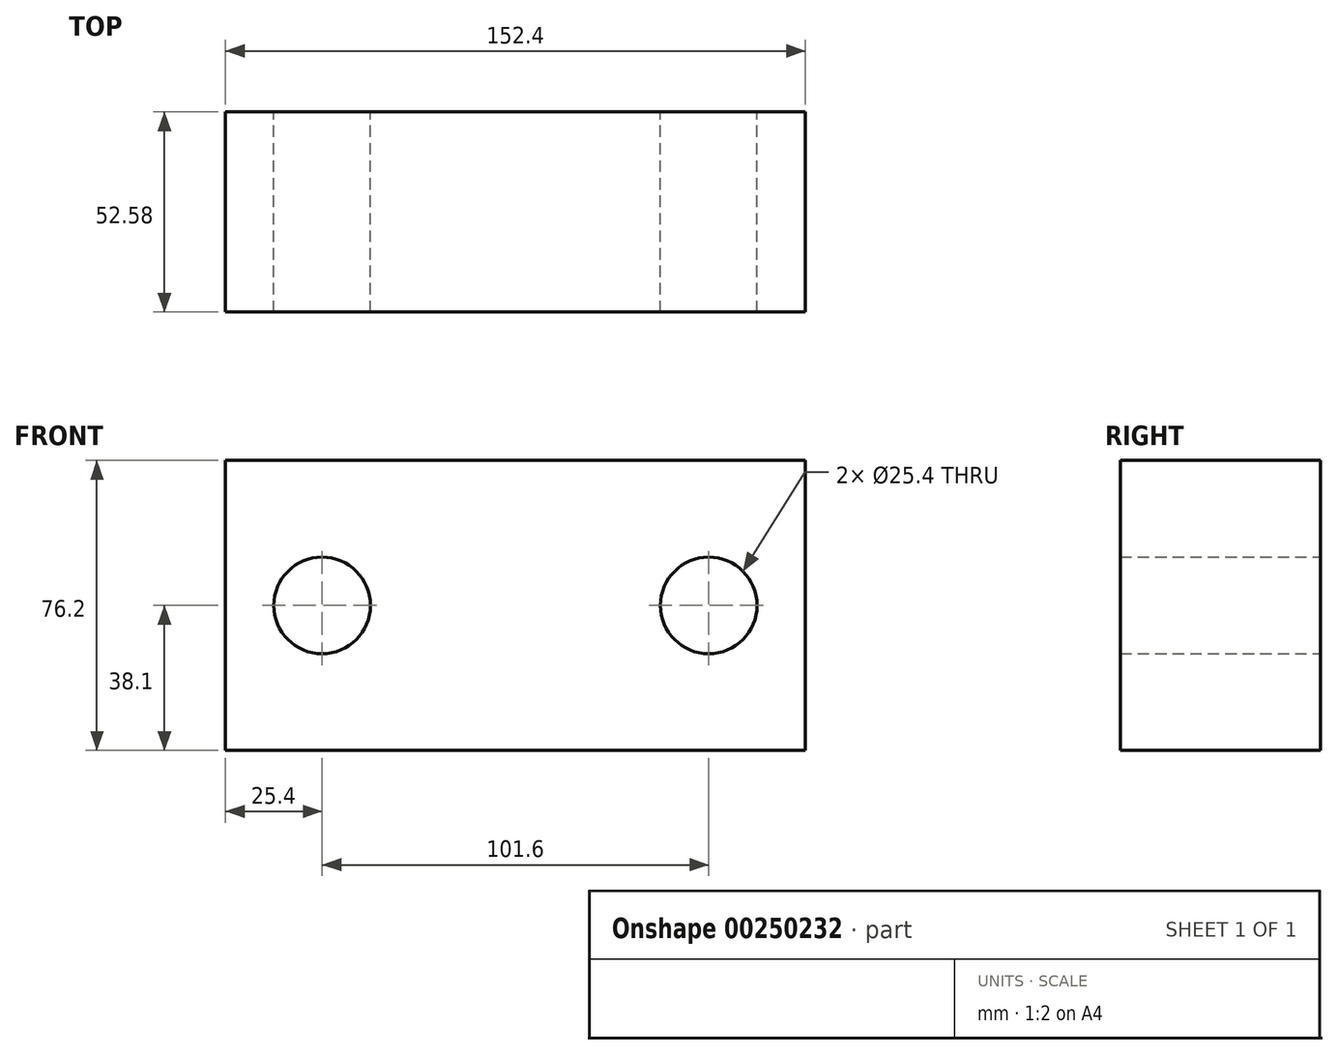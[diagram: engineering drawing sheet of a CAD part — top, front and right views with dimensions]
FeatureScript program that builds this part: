
annotation { "Feature Type Name" : "Feature", "Feature Type Description" : "" }
export const myFeature = defineFeature(function(context is Context, id is Id, definition is map)
    precondition{}
    {
        {
            var Q0;
            Q0=qCreatedBy(makeId("Front.planeOp"),FACE);
            var sketch = newSketch(context, id + "F0", { "sketchPlane" : qUnion([Q0])});
            skLineSegment(sketch, "E0.bottom", {"start": v(76.2, 38.1) * mm, "end": v(-76.2, 38.1) * mm});
            skLineSegment(sketch, "E0.top", {"start": v(76.2, -38.1) * mm, "end": v(-76.2, -38.1) * mm});
            skLineSegment(sketch, "E0.left", {"start": v(76.2, 38.1) * mm, "end": v(76.2, -38.1) * mm});
            skLineSegment(sketch, "E0.right", {"start": v(-76.2, 38.1) * mm, "end": v(-76.2, -38.1) * mm});
            skPoint(sketch, "E0.middle", {"position": v(0, 0) * mm});
            skCircle(sketch, "E1", {"center": v(50.8, 0) * mm, "radius": 12.7 * mm});
            skCircle(sketch, "E2", {"center": v(-50.8, 0) * mm, "radius": 12.7 * mm});
            skSolve(sketch);
        }
        {
            var Q0;
            Q0=qCreatedBy(makeId("Top.planeOp"),FACE);
            var sketch = newSketch(context, id + "F1", { "sketchPlane" : qUnion([Q0])});
            skLineSegment(sketch, "E3.bottom", {"start": v(0, -15.87) * mm, "end": v(-12.7, -15.88) * mm});
            skLineSegment(sketch, "E3.top", {"start": v(0, -9.53) * mm, "end": v(-12.7, -9.53) * mm});
            skLineSegment(sketch, "E3.left", {"start": v(0, -15.87) * mm, "end": v(0, -9.52) * mm});
            skLineSegment(sketch, "E3.right", {"start": v(-12.7, -15.88) * mm, "end": v(-12.7, -9.53) * mm});
            skSolve(sketch);
        }
        {
            var Q0;
            Q0=makeQuery(id+"F0.imprint","IMPRINT",FACE,{"disambiguationData":[TD([[makeQuery(id+"F0.imprint","IMPRINT",EDGE,{"derivedFrom":sQuery(id+"F0.wireOp",EDGE,"E0.bottom")}),1.0]])]});
            extrude(context, id + "F2", {"entities" : qUnion([Q0]), "depth" : 52.58 * mm});
        }
        {
            var Q0;
            Q0=sQuery(id+"F1.wireOp",EDGE,"E3.bottom");
            var Q1;
            Q1=sQuery(id+"F1.wireOp",EDGE,"E3.top");
            var Q2;
            Q2=sQuery(id+"F1.wireOp",EDGE,"E3.left");
            var Q3;
            Q3=sQuery(id+"F1.wireOp",EDGE,"E3.right");
            extrude(context, id + "F3", {"bodyType" : ToolBodyType.SURFACE, "surfaceEntities" : qUnion([Q0, Q1, Q2, Q3]), "depth" : 75.95 * mm});
        }
    });
